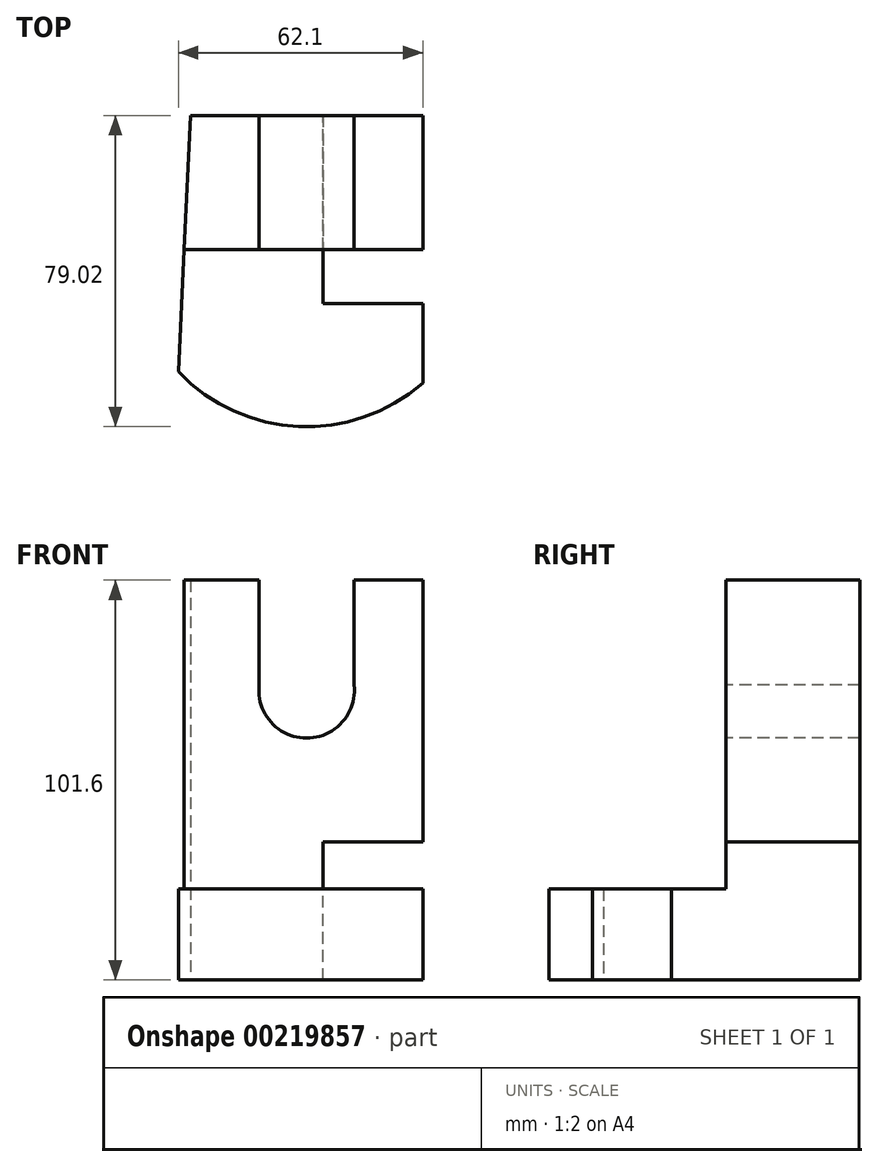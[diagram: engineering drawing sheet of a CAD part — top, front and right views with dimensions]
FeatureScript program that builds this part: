
annotation { "Feature Type Name" : "Feature", "Feature Type Description" : "" }
export const myFeature = defineFeature(function(context is Context, id is Id, definition is map)
    precondition{}
    {
        {
            var Q0;
            Q0=qCreatedBy(makeId("Top.planeOp"),FACE);
            var sketch = newSketch(context, id + "F0", { "sketchPlane" : qUnion([Q0])});
            skCircle(sketch, "E0", {"center": v(0, 0) * mm, "radius": 45.03 * mm});
            skSolve(sketch);
        }
        {
            var Q0;
            Q0 = qSketchRegion(id + "F0", true);
            extrude(context, id + "F1", {"entities" : qUnion([Q0]), "depth" : 101.6 * mm});
        }
        {
            var Q0;
            Q0=makeQuery(id+"F1.opExtrude","CAP_FACE",FACE,{"disambiguationData":[OSD([sQuery(id+"F0.wireOp",EDGE,"E0")])],"isStart":false});
            var sketch = newSketch(context, id + "F2", { "sketchPlane" : qUnion([Q0])});
            skLineSegment(sketch, "E1", {"start": v(-45.03, 0) * mm, "end": v(45.03, 0) * mm});
            skLineSegment(sketch, "E2", {"start": v(45.03, 0) * mm, "end": v(161.7, -116.24) * mm});
            skLineSegment(sketch, "E3", {"start": v(161.7, -116.24) * mm, "end": v(45.03, -116.24) * mm});
            skLineSegment(sketch, "E4", {"start": v(45.03, -116.24) * mm, "end": v(-69.55, 0) * mm});
            skLineSegment(sketch, "E5", {"start": v(-69.55, 0) * mm, "end": v(-45.03, 0) * mm});
            skSolve(sketch);
        }
        {
            var Q0;
            Q0 = qSketchRegion(id + "F2", true);
            extrude(context, id + "F3", {"entities" : qUnion([Q0]), "operationType" : NewBodyOperationType.REMOVE, "oppositeDirection" : true, "depth" : 78.49 * mm});
        }
        {
            var Q0;
            Q0=makeQuery(id+"F1.opExtrude","CAP_FACE",FACE,{"disambiguationData":[OSD([sQuery(id+"F0.wireOp",EDGE,"E0")])],"isStart":false});
            var sketch = newSketch(context, id + "F4", { "sketchPlane" : qUnion([Q0])});
            skLineSegment(sketch, "E6", {"start": v(-25.68, -59.28) * mm, "end": v(-61.14, -57.63) * mm});
            skLineSegment(sketch, "E7", {"start": v(-61.14, -57.63) * mm, "end": v(-55.67, 59.53) * mm});
            skLineSegment(sketch, "E8", {"start": v(-55.67, 59.53) * mm, "end": v(-21.06, 57.92) * mm});
            skLineSegment(sketch, "E9", {"start": v(-33.87, -58.9) * mm, "end": v(-28.4, 58.26) * mm});
            skSolve(sketch);
        }
        {
            var Q0;
            Q0 = qSketchRegion(id + "F4", true);
            extrude(context, id + "F5", {"entities" : qUnion([Q0]), "operationType" : NewBodyOperationType.REMOVE, "oppositeDirection" : true, "depth" : 107.19 * mm});
        }
        {
            var Q0;
            Q0=makeQuery(id+"F1.opExtrude","CAP_FACE",FACE,{"disambiguationData":[OSD([sQuery(id+"F0.wireOp",EDGE,"E0")])],"isStart":false});
            var sketch = newSketch(context, id + "F6", { "sketchPlane" : qUnion([Q0])});
            skLineSegment(sketch, "E10", {"start": v(-29.53, 34) * mm, "end": v(29.53, 34) * mm});
            skLineSegment(sketch, "E11", {"start": v(29.53, 34) * mm, "end": v(29.53, -32.53) * mm});
            skLineSegment(sketch, "E12", {"start": v(29.53, -32.53) * mm, "end": v(45.03, -32.53) * mm});
            skLineSegment(sketch, "E13", {"start": v(45.03, -32.53) * mm, "end": v(45.03, 59.28) * mm});
            skLineSegment(sketch, "E14", {"start": v(45.03, 59.28) * mm, "end": v(-29.53, 53.18) * mm});
            skLineSegment(sketch, "E15", {"start": v(-29.53, 53.18) * mm, "end": v(-29.53, 34) * mm});
            skSolve(sketch);
        }
        {
            var Q0;
            Q0 = qSketchRegion(id + "F6", true);
            extrude(context, id + "F7", {"entities" : qUnion([Q0]), "operationType" : NewBodyOperationType.REMOVE, "oppositeDirection" : true, "depth" : 186.94 * mm});
        }
        {
            var Q0;
            Q0=makeQuery(id+"F3.boolean.opBoolean","COPY",FACE,{"derivedFrom":makeQuery(id+"F3.opExtrude","SWEPT_FACE",FACE,{"disambiguationData":[OSD([sQuery(id+"F2.wireOp",EDGE,"E1"),sQuery(id+"F2.wireOp",EDGE,"E5")])]})});
            var sketch = newSketch(context, id + "F8", { "sketchPlane" : qUnion([Q0])});
            skCircle(sketch, "E16", {"center": v(0, 73.57) * mm, "radius": 12.13 * mm});
            skSolve(sketch);
        }
        {
            var Q0;
            Q0 = qSketchRegion(id + "F8", true);
            extrude(context, id + "F9", {"entities" : qUnion([Q0]), "operationType" : NewBodyOperationType.REMOVE, "oppositeDirection" : true, "depth" : 81.03 * mm});
        }
        {
            var Q0;
            Q0=makeQuery(id+"F3.boolean.opBoolean","COPY",FACE,{"derivedFrom":makeQuery(id+"F3.opExtrude","SWEPT_FACE",FACE,{"disambiguationData":[OSD([sQuery(id+"F2.wireOp",EDGE,"E1"),sQuery(id+"F2.wireOp",EDGE,"E5")])]})});
            var sketch = newSketch(context, id + "F10", { "sketchPlane" : qUnion([Q0])});
            skLineSegment(sketch, "E17", {"start": v(12.06, 72.25) * mm, "end": v(-12.06, 72.25) * mm});
            skLineSegment(sketch, "E18", {"start": v(-12.06, 72.25) * mm, "end": v(-12.06, 106.92) * mm});
            skLineSegment(sketch, "E19", {"start": v(-12.06, 106.92) * mm, "end": v(13.07, 106.92) * mm});
            skLineSegment(sketch, "E20", {"start": v(12.06, 72.25) * mm, "end": v(12.06, 128.12) * mm});
            skSolve(sketch);
        }
        {
            var Q0;
            Q0 = qSketchRegion(id + "F10", true);
            extrude(context, id + "F11", {"entities" : qUnion([Q0]), "operationType" : NewBodyOperationType.REMOVE, "oppositeDirection" : true, "depth" : 128.78 * mm});
        }
        {
            var Q0;
            Q0=makeQuery(id+"F7.boolean.opBoolean","COPY",FACE,{"derivedFrom":makeQuery(id+"F7.opExtrude","SWEPT_FACE",FACE,{"disambiguationData":[OSD([sQuery(id+"F6.wireOp",EDGE,"E11")])]})});
            var sketch = newSketch(context, id + "F12", { "sketchPlane" : qUnion([Q0])});
            skLineSegment(sketch, "E21", {"start": v(-16.27, 23.11) * mm, "end": v(-67.44, 30.69) * mm});
            skLineSegment(sketch, "E22", {"start": v(-67.44, 30.69) * mm, "end": v(-70.59, 9.38) * mm});
            skLineSegment(sketch, "E23", {"start": v(-70.59, 9.38) * mm, "end": v(-70.59, -6.55) * mm});
            skLineSegment(sketch, "E24", {"start": v(-70.59, -6.55) * mm, "end": v(0, -13.36) * mm});
            skLineSegment(sketch, "E25", {"start": v(0, -13.36) * mm, "end": v(-16.27, 23.11) * mm});
            skSolve(sketch);
        }
        {
            var Q0;
            Q0 = qSketchRegion(id + "F12", true);
            extrude(context, id + "F13", {"entities" : qUnion([Q0]), "operationType" : NewBodyOperationType.REMOVE, "depth" : 25.4 * mm});
        }
        {
            var Q0;
            Q0=makeQuery(id+"F13.boolean.opBoolean","MERGE",FACE,{"derivedFrom":[makeQuery(id+"F7.boolean.opBoolean","COPY",FACE,{"derivedFrom":makeQuery(id+"F7.opExtrude","SWEPT_FACE",FACE,{"disambiguationData":[OSD([sQuery(id+"F6.wireOp",EDGE,"E11")])]})}),makeQuery(id+"F13.opExtrude","CAP_FACE",FACE,{"disambiguationData":[OSD([sQuery(id+"F12.wireOp",EDGE,"E21"),sQuery(id+"F12.wireOp",EDGE,"E22"),sQuery(id+"F12.wireOp",EDGE,"E23"),sQuery(id+"F12.wireOp",EDGE,"E24"),sQuery(id+"F12.wireOp",EDGE,"E25")])],"isStart":true})]});
            var sketch = newSketch(context, id + "F14", { "sketchPlane" : qUnion([Q0])});
            skLineSegment(sketch, "E26.bottom", {"start": v(13.36, 0) * mm, "end": v(-13.83, 0) * mm});
            skLineSegment(sketch, "E26.top", {"start": v(13.36, 35.05) * mm, "end": v(-13.83, 35.05) * mm});
            skLineSegment(sketch, "E26.left", {"start": v(13.36, 0) * mm, "end": v(13.36, 35.05) * mm});
            skLineSegment(sketch, "E26.right", {"start": v(-13.83, 0) * mm, "end": v(-13.83, 35.05) * mm});
            skLineSegment(sketch, "E27", {"start": v(13.36, 35.05) * mm, "end": v(53.8, 35.05) * mm});
            skLineSegment(sketch, "E28", {"start": v(53.8, 35.05) * mm, "end": v(53.8, 0) * mm});
            skLineSegment(sketch, "E29", {"start": v(53.8, 0) * mm, "end": v(20, 0) * mm});
            skLineSegment(sketch, "E30", {"start": v(13.36, 0) * mm, "end": v(20, 0) * mm});
            skSolve(sketch);
        }
        {
            var Q0;
            Q0 = qSketchRegion(id + "F14", true);
            extrude(context, id + "F15", {"entities" : qUnion([Q0]), "operationType" : NewBodyOperationType.REMOVE, "oppositeDirection" : true, "depth" : 25.4 * mm});
        }
    });
